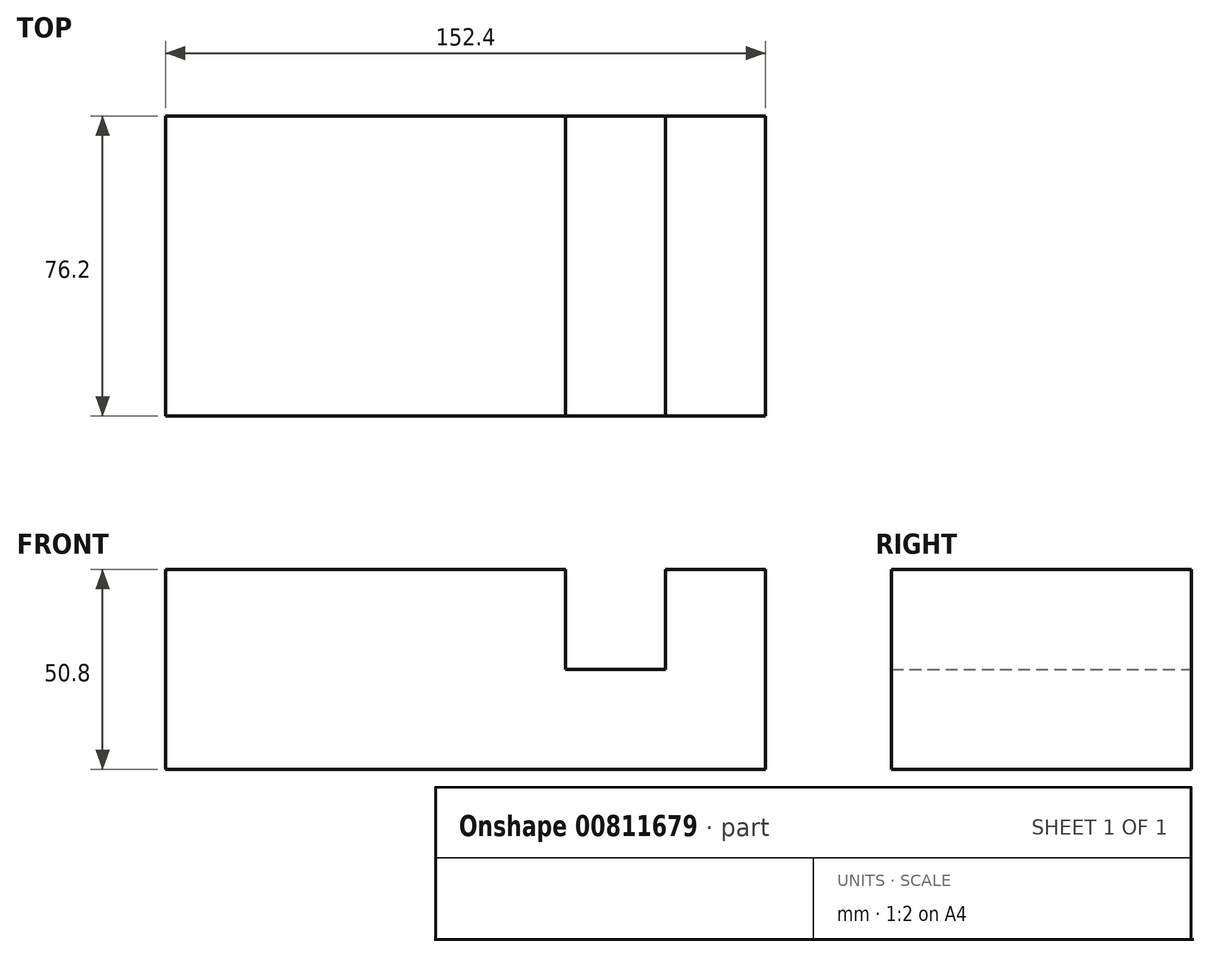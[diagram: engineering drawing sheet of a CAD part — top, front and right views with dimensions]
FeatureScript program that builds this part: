
annotation { "Feature Type Name" : "Feature", "Feature Type Description" : "" }
export const myFeature = defineFeature(function(context is Context, id is Id, definition is map)
    precondition{}
    {
        {
            var Q0;
            Q0=qCreatedBy(makeId("Front.planeOp"),FACE);
            var sketch = newSketch(context, id + "F0", { "sketchPlane" : qUnion([Q0])});
            skLineSegment(sketch, "E0.bottom", {"start": v(-101.6, 50.8) * mm, "end": v(0, 50.8) * mm});
            skLineSegment(sketch, "E0.top", {"start": v(-101.6, 0) * mm, "end": v(0, 0) * mm});
            skLineSegment(sketch, "E0.left", {"start": v(-101.6, 50.8) * mm, "end": v(-101.6, 0) * mm});
            skLineSegment(sketch, "E0.right", {"start": v(0, 50.8) * mm, "end": v(0, 0) * mm});
            skLineSegment(sketch, "E1.bottom", {"start": v(0, 25.4) * mm, "end": v(25.4, 25.4) * mm});
            skLineSegment(sketch, "E1.top", {"start": v(0, 0) * mm, "end": v(25.4, 0) * mm});
            skLineSegment(sketch, "E1.left", {"start": v(0, 25.4) * mm, "end": v(0, 0) * mm});
            skLineSegment(sketch, "E1.right", {"start": v(25.4, 25.4) * mm, "end": v(25.4, 0) * mm});
            skLineSegment(sketch, "E2.bottom", {"start": v(25.4, 0) * mm, "end": v(50.8, 0) * mm});
            skLineSegment(sketch, "E2.top", {"start": v(25.4, 50.8) * mm, "end": v(50.8, 50.8) * mm});
            skLineSegment(sketch, "E2.left", {"start": v(25.4, 0) * mm, "end": v(25.4, 50.8) * mm});
            skLineSegment(sketch, "E2.right", {"start": v(50.8, 0) * mm, "end": v(50.8, 50.8) * mm});
            skSolve(sketch);
        }
        {
            var Q0;
            Q0 = qSketchRegion(id + "F0", true);
            extrude(context, id + "F1", {"entities" : qUnion([Q0]), "depth" : 76.2 * mm, "offsetDistance" : 25.4 * mm});
        }
    });
